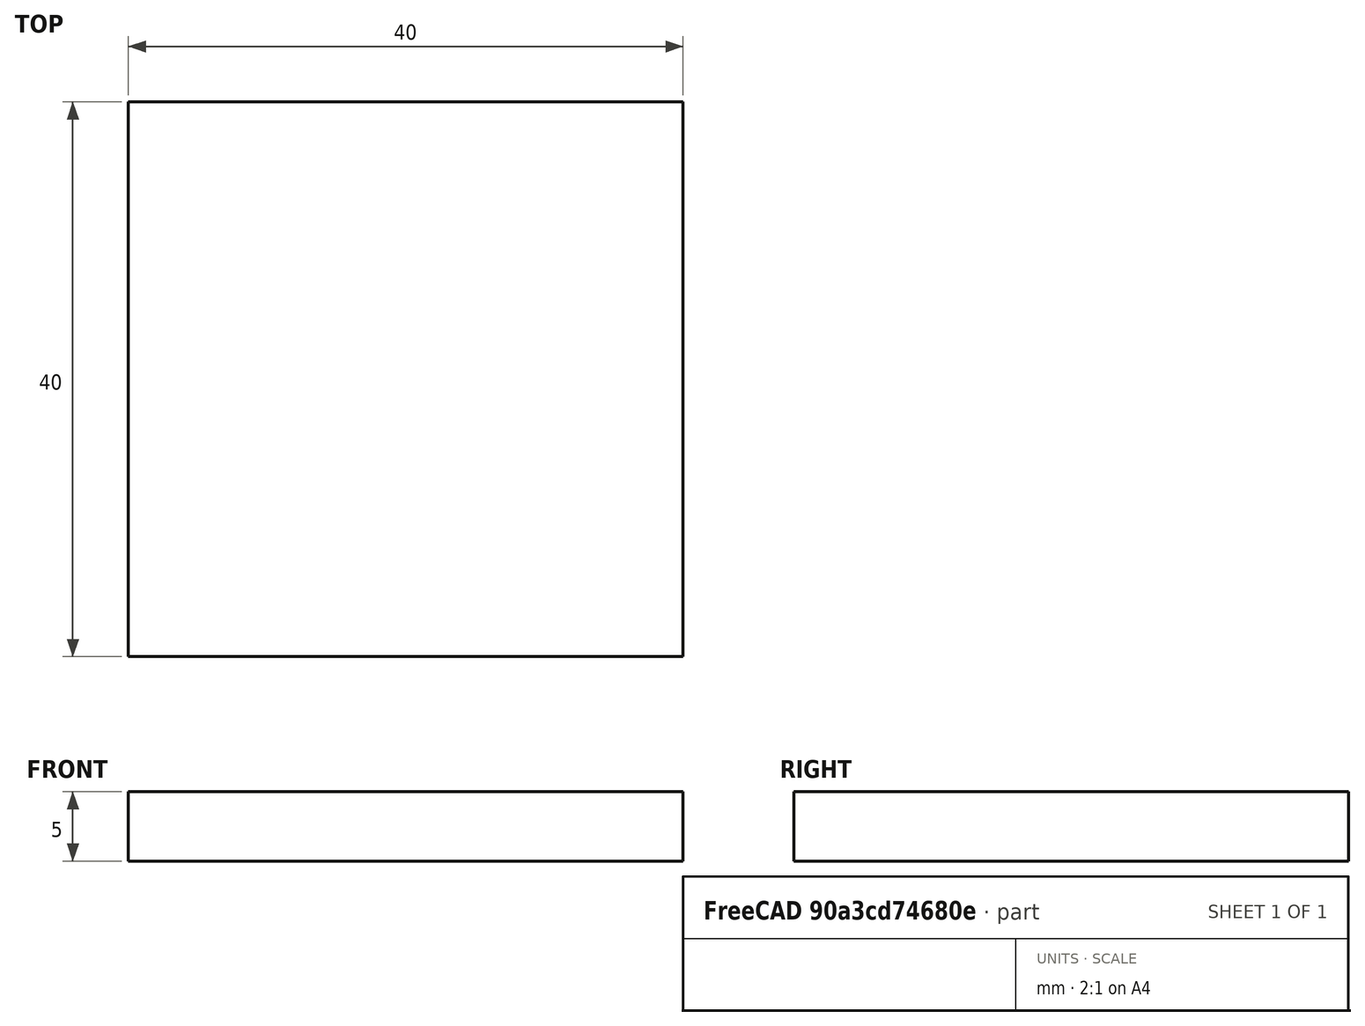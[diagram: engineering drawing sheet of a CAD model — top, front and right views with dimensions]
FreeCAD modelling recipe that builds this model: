
FCSTD DOCUMENT  (FreeCAD 0.17R13541 (Git))
Label: 40x40x5square
License: All rights reserved
LicenseURL: http://en.wikipedia.org/wiki/All_rights_reserved
objects: Sketcher::SketchObject×1, Part::Extrusion×1
note: 2 computed .brp shape members not serialized (recipe doc carries the construction recipe); baked Part::Feature solids carry a one-line shape summary decoded from their .brp

FEATURE [Sketcher::SketchObject] Sketch
  sketch-geometry (4):
    g0: LineSegment StartX=-8.37634 StartY=30.5315 StartZ=0 EndX=31.6237 EndY=30.5315 EndZ=0
    g1: LineSegment StartX=31.6237 StartY=30.5315 StartZ=0 EndX=31.6237 EndY=-9.46853 EndZ=0
    g2: LineSegment StartX=31.6237 StartY=-9.46853 StartZ=0 EndX=-8.37634 EndY=-9.46853 EndZ=0
    g3: LineSegment StartX=-8.37634 StartY=-9.46853 StartZ=0 EndX=-8.37634 EndY=30.5315 EndZ=0
  constraints (12):
    c: Coincident(g0,g1)
    c: Coincident(g1,g2)
    c: Coincident(g2,g3)
    c: Coincident(g3,g0)
    c: Horizontal(g0)
    c: Horizontal(g2)
    c: Vertical(g1)
    c: Vertical(g3)
    c: Equal(g0,g1)
    c: Equal(g1,g2)
    c: Equal(g2,g3)
    c: Distance(g0) = 40
FEATURE [Part::Extrusion] Extrude
  Base = -> Sketch
  Dir = (0,0,1)
  DirMode = 2
  FaceMakerClass = Part::FaceMakerBullseye
  LengthFwd = 5
  LengthRev = 0
  Solid = true
  Symmetric = false
